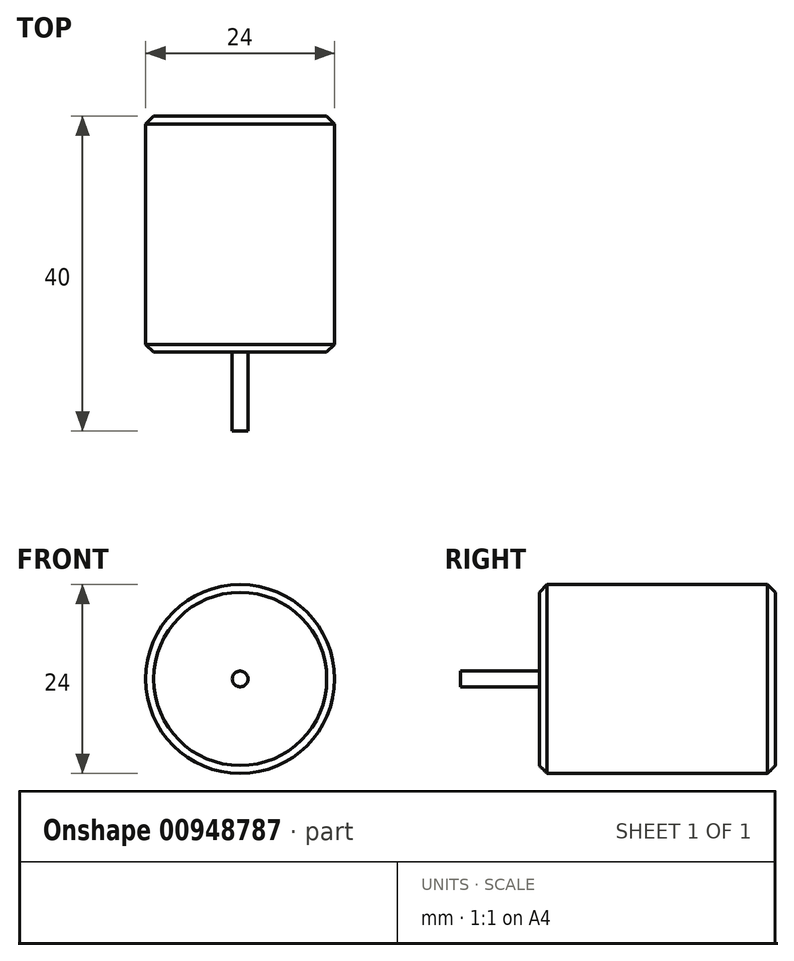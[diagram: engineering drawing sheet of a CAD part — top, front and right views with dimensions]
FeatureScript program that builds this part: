
annotation { "Feature Type Name" : "Feature", "Feature Type Description" : "" }
export const myFeature = defineFeature(function(context is Context, id is Id, definition is map)
    precondition{}
    {
        {
            var Q0;
            Q0=qCreatedBy(makeId("Front.planeOp"),FACE);
            var sketch = newSketch(context, id + "F0", { "sketchPlane" : qUnion([Q0])});
            skCircle(sketch, "E0", {"center": v(0, 0) * mm, "radius": 12 * mm});
            skSolve(sketch);
        }
        {
            var Q0;
            Q0=makeQuery(id+"F0.imprint","IMPRINT",FACE,{"disambiguationData":[TD([[makeQuery(id+"F0.imprint","IMPRINT",EDGE,{"derivedFrom":sQuery(id+"F0.wireOp",EDGE,"E0")}),1.0]])]});
            extrude(context, id + "F1", {"entities" : qUnion([Q0]), "depth" : 30 * mm, "offsetDistance" : 25 * mm});
        }
        {
            var Q0;
            Q0=makeQuery(id+"F1.opExtrude","CAP_EDGE",EDGE,{"disambiguationData":[OSD([sQuery(id+"F0.wireOp",EDGE,"E0")])],"isStart":false});
            var Q1;
            Q1=makeQuery(id+"F1.opExtrude","CAP_EDGE",EDGE,{"disambiguationData":[OSD([sQuery(id+"F0.wireOp",EDGE,"E0")])],"isStart":true});
            chamfer(context, id + "F2", {"entities" : qUnion([Q0, Q1]), "width" : 1 * mm, "tangentPropagation" : true});
        }
        {
            var Q0;
            Q0=makeQuery(id+"F1.opExtrude","CAP_FACE",FACE,{"disambiguationData":[OSD([sQuery(id+"F0.wireOp",EDGE,"E0")])],"isStart":false});
            var sketch = newSketch(context, id + "F3", { "sketchPlane" : qUnion([Q0])});
            skCircle(sketch, "E1", {"center": v(0, 0) * mm, "radius": 1 * mm});
            skSolve(sketch);
        }
        {
            var Q0;
            Q0=makeQuery(id+"F3.imprint","IMPRINT",FACE,{"disambiguationData":[TD([[makeQuery(id+"F3.imprint","IMPRINT",EDGE,{"derivedFrom":sQuery(id+"F3.wireOp",EDGE,"E1")}),1.0]])]});
            extrude(context, id + "F4", {"entities" : qUnion([Q0]), "depth" : 10 * mm, "offsetDistance" : 25 * mm});
        }
    });
